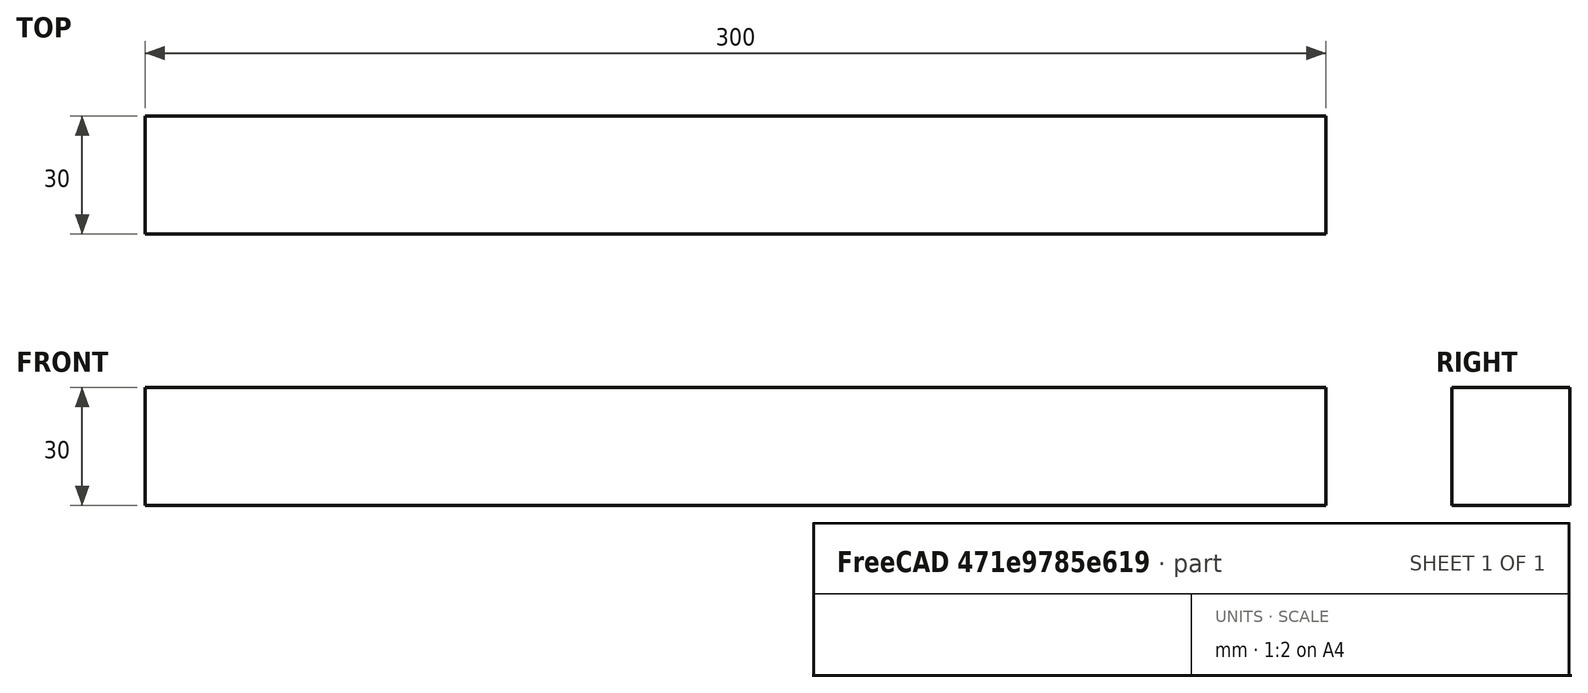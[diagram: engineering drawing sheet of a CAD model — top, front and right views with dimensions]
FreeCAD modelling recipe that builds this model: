
FCSTD DOCUMENT  (FreeCAD 0.20R29177 (Git))
Label: framerear
License: All rights reserved
LicenseURL: http://en.wikipedia.org/wiki/All_rights_reserved
objects: Sketcher::SketchObject×1, PartDesign::Pad×1, PartDesign::Body×1
note: 4 computed .brp shape members not serialized (recipe doc carries the construction recipe); baked Part::Feature solids carry a one-line shape summary decoded from their .brp

FEATURE [Sketcher::SketchObject] Sketch
  FullyConstrained = true
  MapMode = 5
  Placement = pos=(0,0,0) rot=(0.57735,0.57735,0.57735;2.0944rad)
  Support = -> [YZ_Plane]
  sketch-geometry (4):
    g0: LineSegment StartX=0 StartY=0 StartZ=0 EndX=30 EndY=0 EndZ=0
    g1: LineSegment StartX=30 StartY=0 StartZ=0 EndX=30 EndY=30 EndZ=0
    g2: LineSegment StartX=30 StartY=30 StartZ=0 EndX=0 EndY=30 EndZ=0
    g3: LineSegment StartX=0 StartY=30 StartZ=0 EndX=0 EndY=0 EndZ=0
  constraints (11):
    c: Coincident(g0,g1)
    c: Coincident(g1,g2)
    c: Coincident(g2,g3)
    c: Coincident(g3,g0)
    c: Horizontal(g0)
    c: Horizontal(g2)
    c: Vertical(g1)
    c: Vertical(g3)
    c: Coincident(g0,g-1)
    c: Equal(g1,g2)
    c: DistanceX(g0,g0) = 30
FEATURE [PartDesign::Pad] Pad
  Direction = (1,1,1)
  Length = 300
  Length2 = 100
  Placement = pos=(0,0,0) rot=(0.57735,0.57735,0.57735;2.0944rad)
  Profile = -> Sketch
  Type = 0
FEATURE [PartDesign::Body] Body  label="framerear"
  Group = -> [Sketch,Pad]
  Origin = -> Origin
  Tip = -> Pad
